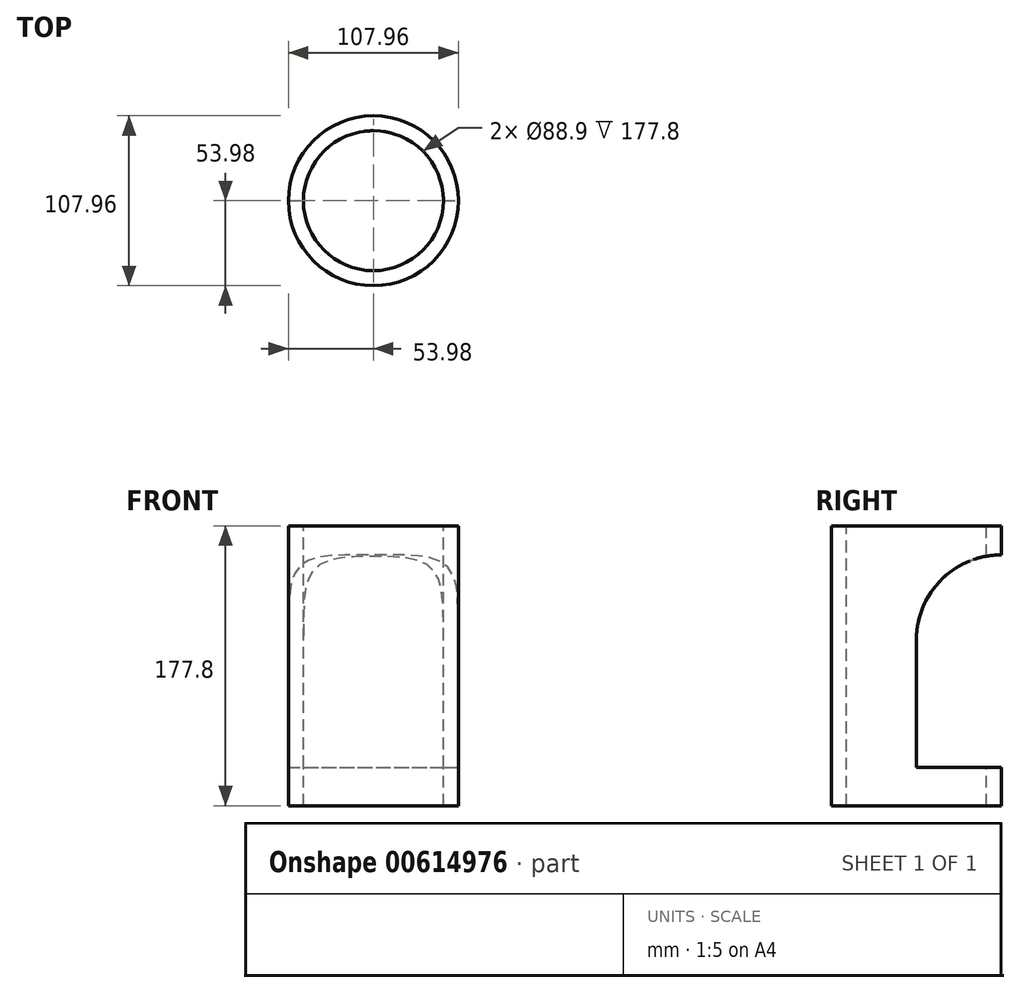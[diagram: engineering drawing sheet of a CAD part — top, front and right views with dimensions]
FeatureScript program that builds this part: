
annotation { "Feature Type Name" : "Feature", "Feature Type Description" : "" }
export const myFeature = defineFeature(function(context is Context, id is Id, definition is map)
    precondition{}
    {
        {
            var Q0;
            Q0=qCreatedBy(makeId("Top.planeOp"),FACE);
            var sketch = newSketch(context, id + "F0", { "sketchPlane" : qUnion([Q0])});
            skCircle(sketch, "E0", {"center": v(0, 0) * mm, "radius": 53.98 * mm});
            skSolve(sketch);
        }
        {
            var Q0;
            Q0=makeQuery(id+"F0.imprint","IMPRINT",FACE,{"disambiguationData":[TD([[makeQuery(id+"F0.imprint","IMPRINT",EDGE,{"derivedFrom":sQuery(id+"F0.wireOp",EDGE,"E0")}),1.0]])]});
            extrude(context, id + "F1", {"entities" : qUnion([Q0]), "depth" : 177.8 * mm, "offsetDistance" : 25.4 * mm});
        }
        {
            var Q0;
            Q0=qCreatedBy(makeId("Right.planeOp"),FACE);
            var sketch = newSketch(context, id + "F2", { "sketchPlane" : qUnion([Q0])});
            skCircle(sketch, "E1", {"center": v(53.98, 105.39) * mm, "radius": 53.97 * mm});
            skLineSegment(sketch, "E2", {"start": v(0, 177.99) * mm, "end": v(0, 0) * mm, "construction": true});
            skLineSegment(sketch, "E3", {"start": v(53.98, 177.8) * mm, "end": v(53.98, 0) * mm});
            skLineSegment(sketch, "E4", {"start": v(-53.98, 0) * mm, "end": v(-53.98, 177.8) * mm});
            skLineSegment(sketch, "E5", {"start": v(0, 24.41) * mm, "end": v(0, 105.39) * mm});
            skLineSegment(sketch, "E6.bottom", {"start": v(0, 105.39) * mm, "end": v(53.98, 105.39) * mm});
            skLineSegment(sketch, "E6.top", {"start": v(0, 24.43) * mm, "end": v(53.98, 24.43) * mm});
            skLineSegment(sketch, "E6.left", {"start": v(0, 105.39) * mm, "end": v(0, 24.43) * mm});
            skLineSegment(sketch, "E6.right", {"start": v(53.98, 105.39) * mm, "end": v(53.98, 24.43) * mm});
            skSolve(sketch);
        }
        {
            var Q0;
            {var subQ4=sQuery(id+"F2.wireOp",EDGE,"E6.top");Q0=makeQuery(id+"F2.imprint","IMPRINT",FACE,{"disambiguationData":[TD([[makeQuery(id+"F2.imprint","IMPRINT",EDGE,{"derivedFrom":subQ4}),1.0]])]});}
            var Q1;
            {var subQ0=sQuery(id+"F2.wireOp",EDGE,"E6.bottom");Q1=makeQuery(id+"F2.imprint","IMPRINT",FACE,{"disambiguationData":[TD([[makeQuery(id+"F2.imprint","IMPRINT",EDGE,{"derivedFrom":subQ0}),1.0]])]});}
            var Q2;
            {var subQ0=sQuery(id+"F2.wireOp",EDGE,"E6.bottom");Q2=makeQuery(id+"F2.imprint","IMPRINT",FACE,{"disambiguationData":[TD([[makeQuery(id+"F2.imprint","IMPRINT",EDGE,{"derivedFrom":subQ0}),-1.0]])]});}
            extrude(context, id + "F3", {"entities" : qUnion([Q0, Q1, Q2]), "operationType" : NewBodyOperationType.REMOVE, "oppositeDirection" : true, "depth" : 78.74 * mm, "offsetDistance" : 25.4 * mm, "hasSecondDirection" : true, "secondDirectionOppositeDirection" : false, "secondDirectionDepth" : 76.2 * mm});
        }
        {
            var Q0;
            Q0=makeQuery(id+"F1.opExtrude","CAP_FACE",FACE,{"disambiguationData":[OSD([sQuery(id+"F0.wireOp",EDGE,"E0")])],"isStart":false});
            var sketch = newSketch(context, id + "F4", { "sketchPlane" : qUnion([Q0])});
            skCircle(sketch, "E7", {"center": v(0, 0) * mm, "radius": 44.45 * mm});
            skSolve(sketch);
        }
        {
            var Q0;
            Q0 = qSketchRegion(id + "F4", true);
            extrude(context, id + "F5", {"entities" : qUnion([Q0]), "operationType" : NewBodyOperationType.REMOVE, "oppositeDirection" : true, "depth" : 259.84 * mm, "offsetDistance" : 25.4 * mm});
        }
    });
